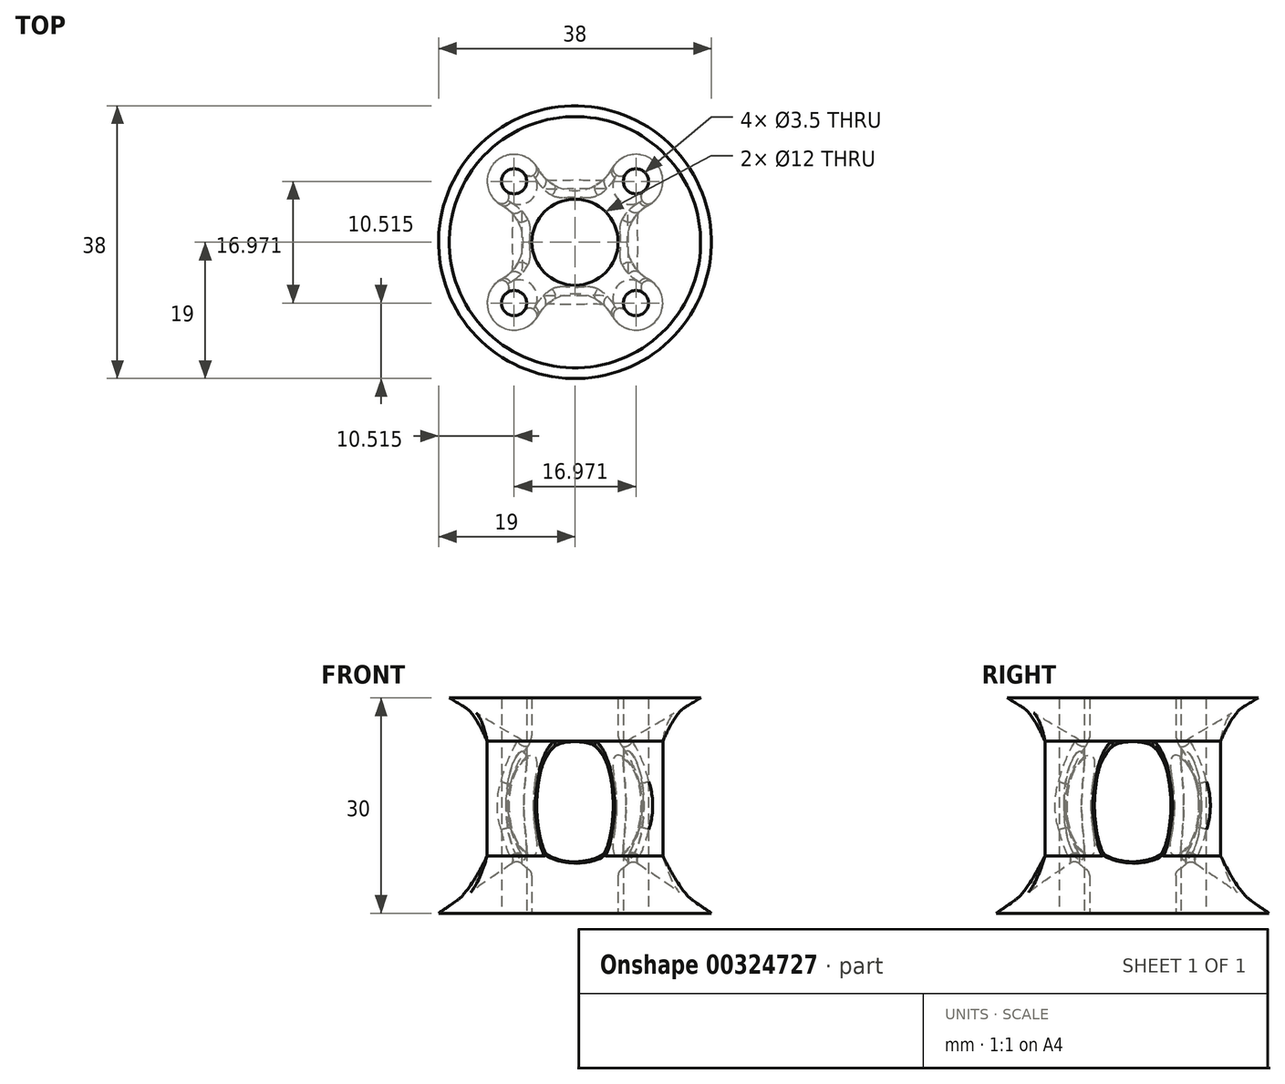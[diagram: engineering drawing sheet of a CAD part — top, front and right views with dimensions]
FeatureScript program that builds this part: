
annotation { "Feature Type Name" : "Feature", "Feature Type Description" : "" }
export const myFeature = defineFeature(function(context is Context, id is Id, definition is map)
    precondition{}
    {
        {
            var Q0;
            Q0=qCreatedBy(makeId("Top.planeOp"),FACE);
            var sketch = newSketch(context, id + "F0", { "sketchPlane" : qUnion([Q0])});
            skCircle(sketch, "E0", {"center": v(0, 0) * mm, "radius": 6 * mm});
            skCircle(sketch, "E1", {"center": v(0, 0) * mm, "radius": 17.5 * mm});
            skCircle(sketch, "E2.0", {"center": v(0, 0) * mm, "radius": 12 * mm, "construction": true});
            skLineSegment(sketch, "E3", {"start": v(0, 0) * mm, "end": v(-17.5, 0) * mm, "construction": true});
            skLineSegment(sketch, "E4", {"start": v(-17.5, 0) * mm, "end": v(0, 0) * mm, "construction": true});
            skLineSegment(sketch, "E5", {"start": v(-12.37, 12.37) * mm, "end": v(12.37, -12.37) * mm, "construction": true});
            skLineSegment(sketch, "E6", {"start": v(12.37, 12.37) * mm, "end": v(-12.37, -12.37) * mm, "construction": true});
            skCircle(sketch, "E7", {"center": v(-8.49, 8.49) * mm, "radius": 1.75 * mm});
            skCircle(sketch, "E8", {"center": v(8.49, 8.49) * mm, "radius": 1.75 * mm});
            skCircle(sketch, "E9", {"center": v(8.49, -8.49) * mm, "radius": 1.75 * mm});
            skCircle(sketch, "E10", {"center": v(-8.49, -8.49) * mm, "radius": 1.75 * mm});
            skSolve(sketch);
        }
        {
            var Q0;
            Q0 = qSketchRegion(id + "F0", true);
            var sketch = newSketch(context, id + "F1", { "sketchPlane" : qUnion([Q0])});
            skCircle(sketch, "E11.0", {"center": v(8.49, 8.49) * mm, "radius": 1.75 * mm});
            skCircle(sketch, "E12.0", {"center": v(0, 0) * mm, "radius": 6 * mm});
            skCircle(sketch, "E13.0", {"center": v(8.49, -8.49) * mm, "radius": 1.75 * mm});
            skCircle(sketch, "E14.0", {"center": v(-8.49, -8.49) * mm, "radius": 1.75 * mm});
            skCircle(sketch, "E15.0", {"center": v(-8.49, 8.49) * mm, "radius": 1.75 * mm});
            skCircle(sketch, "E16.0", {"center": v(8.49, 8.49) * mm, "radius": 3.75 * mm});
            skCircle(sketch, "E17.0", {"center": v(8.49, -8.49) * mm, "radius": 3.75 * mm});
            skCircle(sketch, "E18.0", {"center": v(-8.49, -8.49) * mm, "radius": 3.75 * mm});
            skCircle(sketch, "E19.0", {"center": v(-8.49, 8.49) * mm, "radius": 3.75 * mm});
            skCircle(sketch, "E20.0", {"center": v(0, 0) * mm, "radius": 7.2 * mm, "construction": true});
            skArc(sketch, "E21", {"start": v(-10.28, -5.2) * mm, "mid": v(-7.2, 0) * mm, "end": v(-10.28, 5.2) * mm});
            skArc(sketch, "E22", {"start": v(-5.2, 10.28) * mm, "mid": v(0, 7.2) * mm, "end": v(5.2, 10.28) * mm});
            skArc(sketch, "E23", {"start": v(10.28, 5.2) * mm, "mid": v(7.2, 0) * mm, "end": v(10.28, -5.2) * mm});
            skArc(sketch, "E24", {"start": v(5.2, -10.28) * mm, "mid": v(0, -7.2) * mm, "end": v(-5.2, -10.28) * mm});
            skSolve(sketch);
        }
        {
            var Q0;
            Q0=qCreatedBy(makeId("Top.planeOp"),FACE);
            cPlane(context, id + "F2", {"entities" : qUnion([Q0]), "cplaneType" : CPlaneType.OFFSET, "offset" : 15 * mm, "width" : 150 * mm, "height" : 150 * mm});
        }
        {
            var Q0;
            Q0=qCreatedBy(makeId("Top.planeOp"),FACE);
            cPlane(context, id + "F3", {"entities" : qUnion([Q0]), "cplaneType" : CPlaneType.OFFSET, "offset" : 15 * mm, "oppositeDirection" : true, "width" : 150 * mm, "height" : 150 * mm});
        }
        {
            var Q0;
            Q0=qCreatedBy(id+"F2.planeOp",FACE);
            var sketch = newSketch(context, id + "F4", { "sketchPlane" : qUnion([Q0])});
            skCircle(sketch, "E25", {"center": v(0, 0) * mm, "radius": 17.5 * mm});
            skSolve(sketch);
        }
        {
            var Q0;
            Q0=qCreatedBy(id+"F3.planeOp",FACE);
            var sketch = newSketch(context, id + "F5", { "sketchPlane" : qUnion([Q0])});
            skCircle(sketch, "E26", {"center": v(0, 0) * mm, "radius": 19 * mm});
            skSolve(sketch);
        }
        {
            var Q0;
            Q0=qCreatedBy(id+"F2.planeOp",FACE);
            cPlane(context, id + "F6", {"entities" : qUnion([Q0]), "cplaneType" : CPlaneType.OFFSET, "offset" : 6 * mm, "oppositeDirection" : true, "width" : 150 * mm, "height" : 150 * mm});
        }
        {
            var Q0;
            Q0=qCreatedBy(id+"F6.planeOp",FACE);
            var sketch = newSketch(context, id + "F7", { "sketchPlane" : qUnion([Q0])});
            skArc(sketch, "E27.0", {"start": v(-10.28, -5.2) * mm, "mid": v(-7.2, 0) * mm, "end": v(-10.28, 5.2) * mm});
            skArc(sketch, "E28.0", {"start": v(-5.2, 10.28) * mm, "mid": v(0, 7.2) * mm, "end": v(5.2, 10.28) * mm});
            skArc(sketch, "E29.0", {"start": v(10.28, 5.2) * mm, "mid": v(7.2, 0) * mm, "end": v(10.28, -5.2) * mm});
            skArc(sketch, "E30.0", {"start": v(5.2, -10.28) * mm, "mid": v(0, -7.2) * mm, "end": v(-5.2, -10.28) * mm});
            skArc(sketch, "E31.0", {"start": v(-10.28, -5.2) * mm, "mid": v(-11.14, -11.14) * mm, "end": v(-5.2, -10.28) * mm});
            skArc(sketch, "E32.0", {"start": v(5.2, -10.28) * mm, "mid": v(11.14, -11.14) * mm, "end": v(10.28, -5.2) * mm});
            skArc(sketch, "E33.0", {"start": v(10.28, 5.2) * mm, "mid": v(11.14, 11.14) * mm, "end": v(5.2, 10.28) * mm});
            skArc(sketch, "E34.0", {"start": v(-5.2, 10.28) * mm, "mid": v(-11.14, 11.14) * mm, "end": v(-10.28, 5.2) * mm});
            skSolve(sketch);
        }
        {
            var Q0;
            Q0=qCreatedBy(id+"F3.planeOp",FACE);
            cPlane(context, id + "F8", {"entities" : qUnion([Q0]), "cplaneType" : CPlaneType.OFFSET, "offset" : 8 * mm, "width" : 150 * mm, "height" : 150 * mm});
        }
        {
            var Q0;
            Q0=makeQuery(id+"F4.imprint","IMPRINT",FACE,{"disambiguationData":[TD([[makeQuery(id+"F4.imprint","IMPRINT",EDGE,{"derivedFrom":sQuery(id+"F4.wireOp",EDGE,"E25")}),1.0]])]});
            var Q1;
            Q1=makeQuery(id+"F7.imprint","IMPRINT",FACE,{"disambiguationData":[TD([[makeQuery(id+"F7.imprint","IMPRINT",EDGE,{"derivedFrom":sQuery(id+"F7.wireOp",EDGE,"E27.0")}),-1.0]])]});
            loft(context, id + "F9", {"sheetProfilesArray" : [{ "sheetProfileEntities" : qUnion([Q0]) }, { "sheetProfileEntities" : qUnion([Q1]) }]});
        }
        {
            var Q0;
            Q0=qCreatedBy(id+"F8.planeOp",FACE);
            var sketch = newSketch(context, id + "F10", { "sketchPlane" : qUnion([Q0])});
            skArc(sketch, "E35.0", {"start": v(5.2, -10.28) * mm, "mid": v(0, -7.2) * mm, "end": v(-5.2, -10.28) * mm});
            skArc(sketch, "E36.0", {"start": v(5.2, -10.28) * mm, "mid": v(11.14, -11.14) * mm, "end": v(10.28, -5.2) * mm});
            skArc(sketch, "E37.0", {"start": v(10.28, 5.2) * mm, "mid": v(7.2, 0) * mm, "end": v(10.28, -5.2) * mm});
            skArc(sketch, "E38.0", {"start": v(10.28, 5.2) * mm, "mid": v(11.14, 11.14) * mm, "end": v(5.2, 10.28) * mm});
            skArc(sketch, "E39.0", {"start": v(-5.2, 10.28) * mm, "mid": v(0, 7.2) * mm, "end": v(5.2, 10.28) * mm});
            skArc(sketch, "E40.0", {"start": v(-5.2, 10.28) * mm, "mid": v(-11.14, 11.14) * mm, "end": v(-10.28, 5.2) * mm});
            skArc(sketch, "E41.0", {"start": v(-10.28, -5.2) * mm, "mid": v(-7.2, 0) * mm, "end": v(-10.28, 5.2) * mm});
            skArc(sketch, "E42.0", {"start": v(-10.28, -5.2) * mm, "mid": v(-11.14, -11.14) * mm, "end": v(-5.2, -10.28) * mm});
            skSolve(sketch);
        }
        {
            var Q0;
            Q0=makeQuery(id+"F5.imprint","IMPRINT",FACE,{"disambiguationData":[TD([[makeQuery(id+"F5.imprint","IMPRINT",EDGE,{"derivedFrom":sQuery(id+"F5.wireOp",EDGE,"E26")}),1.0]])]});
            var Q1;
            Q1=makeQuery(id+"F10.imprint","IMPRINT",FACE,{"disambiguationData":[TD([[makeQuery(id+"F10.imprint","IMPRINT",EDGE,{"derivedFrom":sQuery(id+"F10.wireOp",EDGE,"E35.0")}),-1.0]])]});
            loft(context, id + "F11", {"sheetProfilesArray" : [{ "sheetProfileEntities" : qUnion([Q0]) }, { "sheetProfileEntities" : qUnion([Q1]) }]});
        }
        {
            var Q0;
            Q0=makeQuery(id+"F1.imprint","IMPRINT",FACE,{"disambiguationData":[TD([[makeQuery(id+"F1.imprint","IMPRINT",EDGE,{"derivedFrom":sQuery(id+"F1.wireOp",EDGE,"E12.0")}),-1.0]])]});
            var Q1;
            Q1=makeQuery(id+"F1.imprint","IMPRINT",FACE,{"disambiguationData":[TD([[makeQuery(id+"F1.imprint","IMPRINT",EDGE,{"derivedFrom":sQuery(id+"F1.wireOp",EDGE,"E13.0")}),-1.0]])]});
            var Q2;
            Q2=makeQuery(id+"F1.imprint","IMPRINT",FACE,{"disambiguationData":[TD([[makeQuery(id+"F1.imprint","IMPRINT",EDGE,{"derivedFrom":sQuery(id+"F1.wireOp",EDGE,"E14.0")}),-1.0]])]});
            var Q3;
            Q3=makeQuery(id+"F1.imprint","IMPRINT",FACE,{"disambiguationData":[TD([[makeQuery(id+"F1.imprint","IMPRINT",EDGE,{"derivedFrom":sQuery(id+"F1.wireOp",EDGE,"E11.0")}),-1.0]])]});
            var Q4;
            Q4=makeQuery(id+"F1.imprint","IMPRINT",FACE,{"disambiguationData":[TD([[makeQuery(id+"F1.imprint","IMPRINT",EDGE,{"derivedFrom":sQuery(id+"F1.wireOp",EDGE,"E15.0")}),-1.0]])]});
            var Q5;
            Q5=makeQuery(id+"F1.imprint","IMPRINT",FACE,{"disambiguationData":[TD([[makeQuery(id+"F1.imprint","IMPRINT",EDGE,{"derivedFrom":sQuery(id+"F1.wireOp",EDGE,"E15.0")}),1.0]])]});
            var Q6;
            Q6=makeQuery(id+"F1.imprint","IMPRINT",FACE,{"disambiguationData":[TD([[makeQuery(id+"F1.imprint","IMPRINT",EDGE,{"derivedFrom":sQuery(id+"F1.wireOp",EDGE,"E12.0")}),1.0]])]});
            var Q7;
            Q7=makeQuery(id+"F1.imprint","IMPRINT",FACE,{"disambiguationData":[TD([[makeQuery(id+"F1.imprint","IMPRINT",EDGE,{"derivedFrom":sQuery(id+"F1.wireOp",EDGE,"E11.0")}),1.0]])]});
            var Q8;
            Q8=makeQuery(id+"F1.imprint","IMPRINT",FACE,{"disambiguationData":[TD([[makeQuery(id+"F1.imprint","IMPRINT",EDGE,{"derivedFrom":sQuery(id+"F1.wireOp",EDGE,"E13.0")}),1.0]])]});
            var Q9;
            Q9=makeQuery(id+"F1.imprint","IMPRINT",FACE,{"disambiguationData":[TD([[makeQuery(id+"F1.imprint","IMPRINT",EDGE,{"derivedFrom":sQuery(id+"F1.wireOp",EDGE,"E14.0")}),1.0]])]});
            var Q10;
            Q10=qCreatedBy(id+"F2.planeOp",FACE);
            var Q11;
            Q11=qCreatedBy(id+"F3.planeOp",FACE);
            extrude(context, id + "F12", {"entities" : qUnion([Q0, Q1, Q2, Q3, Q4, Q5, Q6, Q7, Q8, Q9]), "operationType" : NewBodyOperationType.ADD, "endBound" : BoundingType.UP_TO_SURFACE, "endBoundEntityFace" : qUnion([Q10]), "depth" : 30 * mm, "hasSecondDirection" : true, "secondDirectionBound" : SecondDirectionBoundingType.UP_TO_SURFACE, "secondDirectionOppositeDirection" : true, "secondDirectionBoundEntityFace" : qUnion([Q11]), "secondDirectionDepth" : 25 * mm});
        }
        {
            var Q0;
            Q0=qCreatedBy(makeId("Front.planeOp"),FACE);
            var sketch = newSketch(context, id + "F13", { "sketchPlane" : qUnion([Q0])});
            skArc(sketch, "E43", {"start": v(0, 11) * mm, "mid": v(-11, 0) * mm, "end": v(0, -11) * mm});
            skLineSegment(sketch, "E44", {"start": v(0, 11) * mm, "end": v(0, -11) * mm});
            skSolve(sketch);
        }
        {
            var Q0;
            Q0=makeQuery(id+"F13.imprint","IMPRINT",FACE,{"disambiguationData":[TD([[makeQuery(id+"F13.imprint","IMPRINT",EDGE,{"derivedFrom":sQuery(id+"F13.wireOp",EDGE,"E43")}),1.0]])]});
            var Q1;
            Q1=sQuery(id+"F13.wireOp",EDGE,"E44");
            revolve(context, id + "F14", {"operationType" : NewBodyOperationType.REMOVE, "entities" : qUnion([Q0]), "axis" : qUnion([Q1]), "revolveType" : RevolveType.FULL, "oppositeDirection" : true});
        }
        {
            var Q0;
            Q0=makeQuery(id+"F1.imprint","IMPRINT",FACE,{"disambiguationData":[TD([[makeQuery(id+"F1.imprint","IMPRINT",EDGE,{"derivedFrom":sQuery(id+"F1.wireOp",EDGE,"E14.0")}),1.0]])]});
            var Q1;
            Q1=makeQuery(id+"F1.imprint","IMPRINT",FACE,{"disambiguationData":[TD([[makeQuery(id+"F1.imprint","IMPRINT",EDGE,{"derivedFrom":sQuery(id+"F1.wireOp",EDGE,"E13.0")}),1.0]])]});
            var Q2;
            Q2=makeQuery(id+"F1.imprint","IMPRINT",FACE,{"disambiguationData":[TD([[makeQuery(id+"F1.imprint","IMPRINT",EDGE,{"derivedFrom":sQuery(id+"F1.wireOp",EDGE,"E11.0")}),1.0]])]});
            var Q3;
            Q3=makeQuery(id+"F1.imprint","IMPRINT",FACE,{"disambiguationData":[TD([[makeQuery(id+"F1.imprint","IMPRINT",EDGE,{"derivedFrom":sQuery(id+"F1.wireOp",EDGE,"E15.0")}),1.0]])]});
            var Q4;
            Q4=makeQuery(id+"F1.imprint","IMPRINT",FACE,{"disambiguationData":[TD([[makeQuery(id+"F1.imprint","IMPRINT",EDGE,{"derivedFrom":sQuery(id+"F1.wireOp",EDGE,"E12.0")}),1.0]])]});
            var Q5;
            Q5=makeQuery(id+"F9.opLoft","CAP_FACE",FACE,{"disambiguationData":[OSD([makeQuery(id+"F4.imprint","IMPRINT",FACE,{"disambiguationData":[TD([[makeQuery(id+"F4.imprint","IMPRINT",EDGE,{"derivedFrom":sQuery(id+"F4.wireOp",EDGE,"E25")}),1.0]])]})])],"isStart":true});
            var Q6;
            Q6=makeQuery(id+"F11.opLoft","CAP_FACE",FACE,{"disambiguationData":[OSD([makeQuery(id+"F5.imprint","IMPRINT",FACE,{"disambiguationData":[TD([[makeQuery(id+"F5.imprint","IMPRINT",EDGE,{"derivedFrom":sQuery(id+"F5.wireOp",EDGE,"E26")}),1.0]])]})])],"isStart":true});
            extrude(context, id + "F15", {"entities" : qUnion([Q0, Q1, Q2, Q3, Q4]), "operationType" : NewBodyOperationType.REMOVE, "endBound" : BoundingType.UP_TO_SURFACE, "endBoundEntityFace" : qUnion([Q5]), "depth" : 25 * mm, "hasSecondDirection" : true, "secondDirectionBound" : SecondDirectionBoundingType.UP_TO_SURFACE, "secondDirectionOppositeDirection" : true, "secondDirectionBoundEntityFace" : qUnion([Q6]), "secondDirectionDepth" : 25 * mm});
        }
        {
            var Q0;
            Q0=makeQuery(id+"F14.boolean.opBoolean","COPY",FACE,{"derivedFrom":makeQuery(id+"F14.opRevolve","SWEPT_FACE",FACE,{"disambiguationData":[OSD([sQuery(id+"F13.wireOp",EDGE,"E43")])]})});
            var Q1;
            Q1=makeQuery(id+"F15.boolean.opBoolean","COPY",EDGE,{"derivedFrom":makeQuery(id+"F15.opExtrude","TWEAK_EDGE",EDGE,{"derivedFrom":[makeQuery(id+"F1.imprint","IMPRINT",EDGE,{"derivedFrom":sQuery(id+"F1.wireOp",EDGE,"E12.0")}),makeQuery(id+"F9.opLoft","CAP_FACE",FACE,{"disambiguationData":[OSD([makeQuery(id+"F4.imprint","IMPRINT",FACE,{"disambiguationData":[TD([[makeQuery(id+"F4.imprint","IMPRINT",EDGE,{"derivedFrom":sQuery(id+"F4.wireOp",EDGE,"E25")}),1.0]])]})])],"isStart":true})]})});
            var Q2;
            Q2=makeQuery(id+"F15.boolean.opBoolean","COPY",EDGE,{"derivedFrom":makeQuery(id+"F15.opExtrude","TWEAK_EDGE",EDGE,{"derivedFrom":[makeQuery(id+"F1.imprint","IMPRINT",EDGE,{"derivedFrom":sQuery(id+"F1.wireOp",EDGE,"E12.0")}),makeQuery(id+"F11.opLoft","CAP_FACE",FACE,{"disambiguationData":[OSD([makeQuery(id+"F5.imprint","IMPRINT",FACE,{"disambiguationData":[TD([[makeQuery(id+"F5.imprint","IMPRINT",EDGE,{"derivedFrom":sQuery(id+"F5.wireOp",EDGE,"E26")}),1.0]])]})])],"isStart":true})]})});
            fillet(context, id + "F16", {"entities" : qUnion([Q0, Q1, Q2]), "radius" : 1 * mm, "tangentPropagation" : true, "allowEdgeOverflow" : false});
        }
    });
